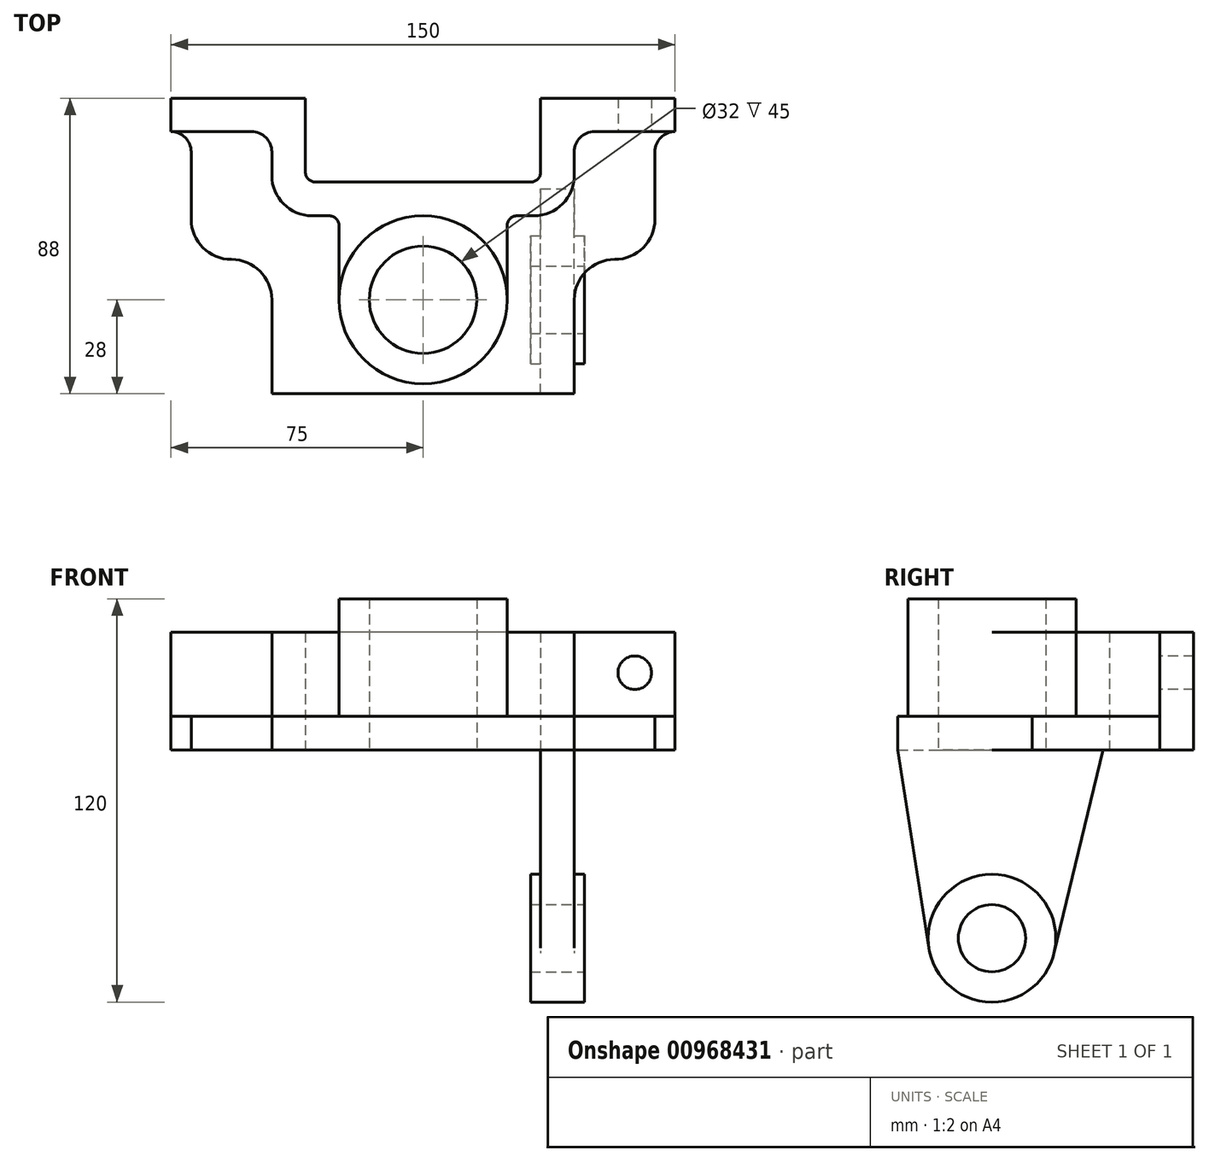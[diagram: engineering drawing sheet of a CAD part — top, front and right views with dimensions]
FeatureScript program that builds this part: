
annotation { "Feature Type Name" : "Feature", "Feature Type Description" : "" }
export const myFeature = defineFeature(function(context is Context, id is Id, definition is map)
    precondition{}
    {
        {
            var Q0;
            Q0=qCreatedBy(makeId("Top.planeOp"),FACE);
            var sketch = newSketch(context, id + "F0", { "sketchPlane" : qUnion([Q0])});
            skCircle(sketch, "E0", {"center": v(0, 0) * mm, "radius": 25 * mm});
            skCircle(sketch, "E1", {"center": v(0, 0) * mm, "radius": 16 * mm});
            skLineSegment(sketch, "E2", {"start": v(0, -28) * mm, "end": v(-45, -28) * mm});
            skLineSegment(sketch, "E3", {"start": v(-45, -28) * mm, "end": v(-45, 0) * mm});
            skLineSegment(sketch, "E4", {"start": v(-57, 12) * mm, "end": v(-57, 12) * mm});
            skLineSegment(sketch, "E5", {"start": v(-69, 24) * mm, "end": v(-69, 44) * mm});
            skLineSegment(sketch, "E6", {"start": v(-51, 50) * mm, "end": v(-75, 50) * mm});
            skLineSegment(sketch, "E7", {"start": v(-75, 50) * mm, "end": v(-75, 60) * mm});
            skLineSegment(sketch, "E8", {"start": v(-75, 60) * mm, "end": v(-35, 60) * mm});
            skLineSegment(sketch, "E9", {"start": v(-35, 60) * mm, "end": v(-35, 38) * mm});
            skLineSegment(sketch, "E10", {"start": v(-32, 35) * mm, "end": v(0, 35) * mm});
            skLineSegment(sketch, "E11", {"start": v(-45, 44) * mm, "end": v(-45, 37) * mm});
            skLineSegment(sketch, "E12", {"start": v(-33, 25) * mm, "end": v(-28, 25) * mm});
            skLineSegment(sketch, "E13", {"start": v(-25, 22) * mm, "end": v(-25, 0) * mm});
            skLineSegment(sketch, "E14.MirrorCS", {"start": v(32, 35) * mm, "end": v(0, 35) * mm});
            skLineSegment(sketch, "E15.MirrorCS", {"start": v(35, 60) * mm, "end": v(35, 38) * mm});
            skLineSegment(sketch, "E16.MirrorCS", {"start": v(75, 60) * mm, "end": v(35, 60) * mm});
            skLineSegment(sketch, "E17.MirrorCS", {"start": v(75, 50) * mm, "end": v(75, 60) * mm});
            skLineSegment(sketch, "E18.MirrorCS", {"start": v(51, 50) * mm, "end": v(75, 50) * mm});
            skLineSegment(sketch, "E19.MirrorCS", {"start": v(45, 44) * mm, "end": v(45, 37) * mm});
            skLineSegment(sketch, "E20.MirrorCS", {"start": v(33, 25) * mm, "end": v(28, 25) * mm});
            skLineSegment(sketch, "E21.MirrorCS", {"start": v(25, 22) * mm, "end": v(25, 0) * mm});
            skLineSegment(sketch, "E22.MirrorCS", {"start": v(69, 24) * mm, "end": v(69, 44) * mm});
            skLineSegment(sketch, "E23.MirrorCS", {"start": v(57, 12) * mm, "end": v(57, 12) * mm});
            skLineSegment(sketch, "E24.MirrorCS", {"start": v(45, -28) * mm, "end": v(45, 0) * mm});
            skLineSegment(sketch, "E25.MirrorCS", {"start": v(0, -28) * mm, "end": v(45, -28) * mm});
            skPoint(sketch, "E26.visualSharp", {"position": v(-25, 25) * mm});
            skArc(sketch, "E26.filletArc", {"start": v(-25, 22) * mm, "mid": v(-25.88, 24.12) * mm, "end": v(-28, 25) * mm});
            skPoint(sketch, "E27.visualSharp", {"position": v(25, 25) * mm});
            skArc(sketch, "E27.filletArc", {"start": v(28, 25) * mm, "mid": v(25.88, 24.12) * mm, "end": v(25, 22) * mm});
            skPoint(sketch, "E28.visualSharp", {"position": v(-35, 35) * mm});
            skArc(sketch, "E28.filletArc", {"start": v(-35, 38) * mm, "mid": v(-34.12, 35.88) * mm, "end": v(-32, 35) * mm});
            skPoint(sketch, "E29.visualSharp", {"position": v(35, 35) * mm});
            skArc(sketch, "E29.filletArc", {"start": v(32, 35) * mm, "mid": v(34.12, 35.88) * mm, "end": v(35, 38) * mm});
            skPoint(sketch, "E30.visualSharp", {"position": v(45, 25) * mm});
            skArc(sketch, "E30.filletArc", {"start": v(33, 25) * mm, "mid": v(41.49, 28.51) * mm, "end": v(45, 37) * mm});
            skPoint(sketch, "E31.visualSharp", {"position": v(-45, 25) * mm});
            skArc(sketch, "E31.filletArc", {"start": v(-45, 37) * mm, "mid": v(-41.49, 28.51) * mm, "end": v(-33, 25) * mm});
            skPoint(sketch, "E32.visualSharp", {"position": v(45, 12) * mm});
            skArc(sketch, "E32.filletArc", {"start": v(57, 12) * mm, "mid": v(48.51, 8.49) * mm, "end": v(45, 0) * mm});
            skPoint(sketch, "E33.visualSharp", {"position": v(-45, 12) * mm});
            skArc(sketch, "E33.filletArc", {"start": v(-45, 0) * mm, "mid": v(-48.51, 8.49) * mm, "end": v(-57, 12) * mm});
            skPoint(sketch, "E34.visualSharp", {"position": v(-69, 12) * mm});
            skArc(sketch, "E34.filletArc", {"start": v(-69, 24) * mm, "mid": v(-65.49, 15.51) * mm, "end": v(-57, 12) * mm});
            skPoint(sketch, "E35.visualSharp", {"position": v(69, 12) * mm});
            skArc(sketch, "E35.filletArc", {"start": v(57, 12) * mm, "mid": v(65.49, 15.51) * mm, "end": v(69, 24) * mm});
            skPoint(sketch, "E36.visualSharp", {"position": v(-45, 50) * mm});
            skArc(sketch, "E36.filletArc", {"start": v(-45, 44) * mm, "mid": v(-46.76, 48.24) * mm, "end": v(-51, 50) * mm});
            skPoint(sketch, "E37.visualSharp", {"position": v(45, 50) * mm});
            skArc(sketch, "E37.filletArc", {"start": v(51, 50) * mm, "mid": v(46.76, 48.24) * mm, "end": v(45, 44) * mm});
            skArc(sketch, "E38", {"start": v(-69, 44) * mm, "mid": v(-70.76, 48.24) * mm, "end": v(-75, 50) * mm});
            skPoint(sketch, "E39.orphan", {"position": v(-69, 50) * mm});
            skArc(sketch, "E40", {"start": v(75, 50) * mm, "mid": v(70.76, 48.24) * mm, "end": v(69, 44) * mm});
            skPoint(sketch, "E41.orphan", {"position": v(69, 50) * mm});
            skSolve(sketch);
        }
        {
            var Q0;
            Q0=sQuery(id+"F0.wireOp",EDGE,"E24.MirrorCS");
            var Q1;
            Q1=qCreatedBy(makeId("Top.planeOp"),FACE);
            cPlane(context, id + "F1", {"entities" : qUnion([Q0, Q1]), "cplaneType" : CPlaneType.LINE_ANGLE, "offset" : 25 * mm, "angle" : 90 * degree, "width" : 150 * mm, "height" : 150 * mm});
        }
        {
            var Q0;
            Q0=qCreatedBy(id+"F1.planeOp",FACE);
            var sketch = newSketch(context, id + "F2", { "sketchPlane" : qUnion([Q0])});
            skLineSegment(sketch, "E42", {"start": v(28, 0) * mm, "end": v(-33, 0) * mm});
            skLineSegment(sketch, "E43", {"start": v(-33, 0) * mm, "end": v(-18.47, -60.44) * mm});
            skLineSegment(sketch, "E44", {"start": v(28, 0) * mm, "end": v(18.77, -58.94) * mm});
            skCircle(sketch, "E45", {"center": v(0, -56) * mm, "radius": 10 * mm});
            skCircle(sketch, "E46.converted", {"center": v(0, -56) * mm, "radius": 19 * mm});
            skSolve(sketch);
        }
        {
            var Q0;
            Q0=makeQuery(id+"F0.imprint","IMPRINT",FACE,{"disambiguationData":[TD([[makeQuery(id+"F0.imprint","IMPRINT",EDGE,{"derivedFrom":sQuery(id+"F0.wireOp",EDGE,"E2")}),-1.0]])]});
            extrude(context, id + "F3", {"entities" : qUnion([Q0]), "depth" : 10 * mm, "offsetDistance" : 25 * mm});
        }
        {
            var Q0;
            Q0=makeQuery(id+"F0.imprint","IMPRINT",FACE,{"disambiguationData":[TD([[makeQuery(id+"F0.imprint","IMPRINT",EDGE,{"derivedFrom":sQuery(id+"F0.wireOp",EDGE,"E1")}),-1.0]])]});
            extrude(context, id + "F4", {"entities" : qUnion([Q0]), "operationType" : NewBodyOperationType.ADD, "depth" : 45 * mm, "offsetDistance" : 25 * mm});
        }
        {
            var Q0;
            Q0=makeQuery(id+"F0.imprint","IMPRINT",FACE,{"disambiguationData":[TD([[makeQuery(id+"F0.imprint","IMPRINT",EDGE,{"derivedFrom":sQuery(id+"F0.wireOp",EDGE,"E6")}),-1.0]])]});
            extrude(context, id + "F5", {"entities" : qUnion([Q0]), "operationType" : NewBodyOperationType.ADD, "depth" : 35 * mm, "offsetDistance" : 25 * mm});
        }
        {
            var Q0;
            Q0=makeQuery(id+"F2.imprint","IMPRINT",FACE,{"disambiguationData":[TD([[makeQuery(id+"F2.imprint","IMPRINT",EDGE,{"derivedFrom":sQuery(id+"F2.wireOp",EDGE,"E42")}),1.0]])]});
            var Q1;
            Q1=makeQuery(id+"F2.imprint","IMPRINT",FACE,{"disambiguationData":[TD([[makeQuery(id+"F2.imprint","IMPRINT",EDGE,{"derivedFrom":sQuery(id+"F2.wireOp",EDGE,"E45")}),-1.0]])]});
            extrude(context, id + "F6", {"entities" : qUnion([Q0, Q1]), "operationType" : NewBodyOperationType.ADD, "depth" : 10 * mm, "offsetDistance" : 25 * mm});
        }
        {
            var Q0;
            Q0=makeQuery(id+"F2.imprint","IMPRINT",FACE,{"disambiguationData":[TD([[makeQuery(id+"F2.imprint","IMPRINT",EDGE,{"derivedFrom":sQuery(id+"F2.wireOp",EDGE,"E45")}),-1.0]])]});
            extrude(context, id + "F7", {"entities" : qUnion([Q0]), "operationType" : NewBodyOperationType.ADD, "depth" : 13 * mm, "offsetDistance" : 25 * mm, "hasSecondDirection" : true, "secondDirectionOppositeDirection" : true, "secondDirectionDepth" : 3 * mm});
        }
        {
            var Q0;
            Q0=makeQuery(id+"F5.opExtrude","SWEPT_FACE",FACE,{"disambiguationData":[OSD([sQuery(id+"F0.wireOp",EDGE,"E18.MirrorCS")])]});
            var sketch = newSketch(context, id + "F8", { "sketchPlane" : qUnion([Q0])});
            skCircle(sketch, "E47", {"center": v(63, 23) * mm, "radius": 5 * mm});
            skSolve(sketch);
        }
        {
            var Q0;
            Q0=makeQuery(id+"F8.imprint","IMPRINT",FACE,{"disambiguationData":[TD([[makeQuery(id+"F8.imprint","IMPRINT",EDGE,{"derivedFrom":sQuery(id+"F8.wireOp",EDGE,"E47")}),1.0]])]});
            extrude(context, id + "F9", {"entities" : qUnion([Q0]), "operationType" : NewBodyOperationType.REMOVE, "endBound" : BoundingType.THROUGH_ALL, "oppositeDirection" : true, "depth" : 25 * mm, "offsetDistance" : 25 * mm});
        }
    });
